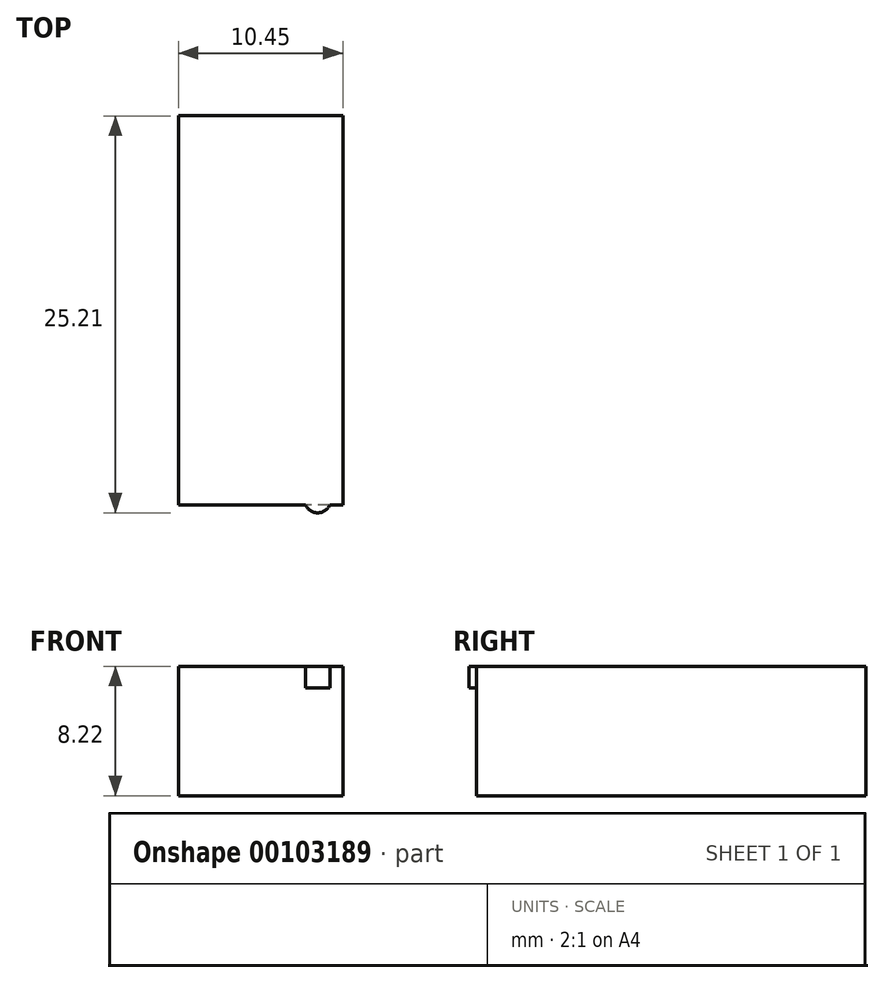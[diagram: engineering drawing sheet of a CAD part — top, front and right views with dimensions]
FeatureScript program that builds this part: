
annotation { "Feature Type Name" : "Feature", "Feature Type Description" : "" }
export const myFeature = defineFeature(function(context is Context, id is Id, definition is map)
    precondition{}
    {
        {
            var Q0;
            Q0=qCreatedBy(makeId("Top.planeOp"),FACE);
            var sketch = newSketch(context, id + "F0", { "sketchPlane" : qUnion([Q0])});
            skLineSegment(sketch, "E0", {"start": v(-32.97, 4.6) * mm, "end": v(-32.97, -20.13) * mm});
            skLineSegment(sketch, "E1", {"start": v(-32.97, 4.6) * mm, "end": v(-22.52, 4.6) * mm});
            skLineSegment(sketch, "E2", {"start": v(-22.52, 4.6) * mm, "end": v(-22.52, -20.13) * mm});
            skLineSegment(sketch, "E3", {"start": v(-32.97, -20.13) * mm, "end": v(-22.52, -20.13) * mm});
            skSolve(sketch);
        }
        {
            var Q0;
            Q0=makeQuery(id+"F0.imprint","IMPRINT",FACE,{"disambiguationData":[TD([[makeQuery(id+"F0.imprint","IMPRINT",EDGE,{"derivedFrom":sQuery(id+"F0.wireOp",EDGE,"E0")}),1.0]])]});
            extrude(context, id + "F1", {"entities" : qUnion([Q0]), "oppositeDirection" : true, "depth" : 8.22 * mm});
        }
        {
            var Q0;
            Q0=qCreatedBy(makeId("Top.planeOp"),FACE);
            var sketch = newSketch(context, id + "F2", { "sketchPlane" : qUnion([Q0])});
            skCircle(sketch, "E4", {"center": v(-24.13, -19.78) * mm, "radius": 0.85 * mm});
            skSolve(sketch);
        }
        {
            var Q0;
            Q0 = qSketchRegion(id + "F2", true);
            extrude(context, id + "F3", {"entities" : qUnion([Q0]), "operationType" : NewBodyOperationType.ADD, "oppositeDirection" : true, "depth" : 1.37 * mm});
        }
    });
